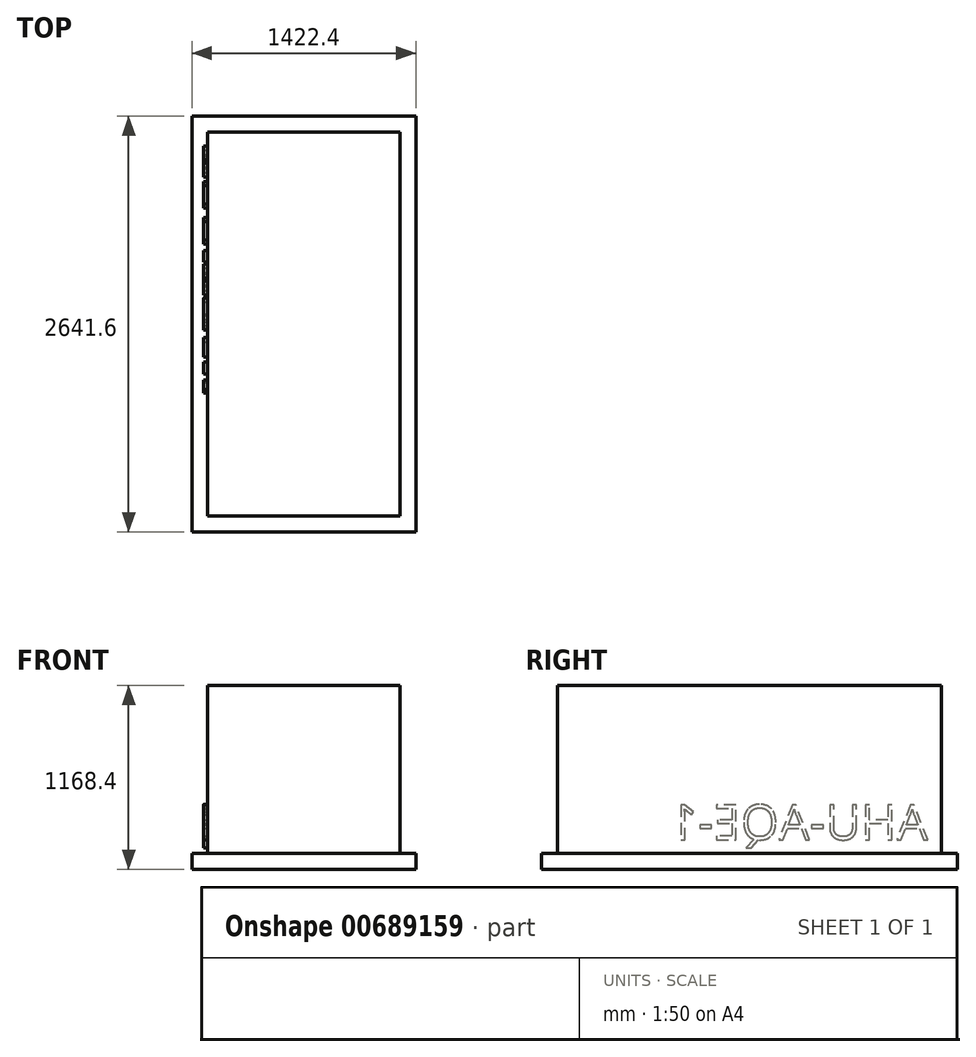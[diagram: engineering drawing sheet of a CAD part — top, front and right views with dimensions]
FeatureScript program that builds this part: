
annotation { "Feature Type Name" : "Feature", "Feature Type Description" : "" }
export const myFeature = defineFeature(function(context is Context, id is Id, definition is map)
    precondition{}
    {
        {
            var Q0;
            Q0=qCreatedBy(makeId("Front.planeOp"),FACE);
            var sketch = newSketch(context, id + "F0", { "sketchPlane" : qUnion([Q0])});
            skLineSegment(sketch, "E0.bottom", {"start": v(-67.53, 1048.52) * mm, "end": v(1151.67, 1048.52) * mm});
            skLineSegment(sketch, "E0.top", {"start": v(-67.53, -18.28) * mm, "end": v(1151.67, -18.28) * mm});
            skLineSegment(sketch, "E0.left", {"start": v(-67.53, 1048.52) * mm, "end": v(-67.53, -18.28) * mm});
            skLineSegment(sketch, "E0.right", {"start": v(1151.67, 1048.52) * mm, "end": v(1151.67, -18.28) * mm});
            skSolve(sketch);
        }
        {
            var Q0;
            Q0=makeQuery(id+"F0.imprint","IMPRINT",FACE,{"disambiguationData":[TD([[makeQuery(id+"F0.imprint","IMPRINT",EDGE,{"derivedFrom":sQuery(id+"F0.wireOp",EDGE,"E0.bottom")}),-1.0]])]});
            extrude(context, id + "F1", {"entities" : qUnion([Q0]), "depth" : 2438.4 * mm, "offsetDistance" : 25.4 * mm});
        }
        {
            var Q0;
            Q0=makeQuery(id+"F1.opExtrude","CAP_FACE",FACE,{"disambiguationData":[OSD([sQuery(id+"F0.wireOp",EDGE,"E0.bottom"),sQuery(id+"F0.wireOp",EDGE,"E0.top"),sQuery(id+"F0.wireOp",EDGE,"E0.left"),sQuery(id+"F0.wireOp",EDGE,"E0.right")])],"isStart":false});
            var sketch = newSketch(context, id + "F2", { "sketchPlane" : qUnion([Q0])});
            skLineSegment(sketch, "E1.bottom", {"start": v(-169.13, -18.28) * mm, "end": v(1253.27, -18.28) * mm});
            skLineSegment(sketch, "E1.top", {"start": v(-169.13, -119.88) * mm, "end": v(1253.27, -119.88) * mm});
            skLineSegment(sketch, "E1.left", {"start": v(-169.13, -18.28) * mm, "end": v(-169.13, -119.88) * mm});
            skLineSegment(sketch, "E1.right", {"start": v(1253.27, -18.28) * mm, "end": v(1253.27, -119.88) * mm});
            skSolve(sketch);
        }
        {
            var Q0;
            Q0=makeQuery(id+"F2.imprint","IMPRINT",FACE,{"disambiguationData":[TD([[makeQuery(id+"F2.imprint","IMPRINT",EDGE,{"derivedFrom":sQuery(id+"F2.wireOp",EDGE,"E1.top")}),1.0]])]});
            extrude(context, id + "F3", {"entities" : qUnion([Q0]), "oppositeDirection" : true, "depth" : 2540 * mm, "offsetDistance" : 25.4 * mm});
        }
        {
            var Q0;
            Q0=makeQuery(id+"F3.opExtrude","CAP_FACE",FACE,{"disambiguationData":[OSD([sQuery(id+"F2.wireOp",EDGE,"E1.bottom"),sQuery(id+"F2.wireOp",EDGE,"E1.top"),sQuery(id+"F2.wireOp",EDGE,"E1.left"),sQuery(id+"F2.wireOp",EDGE,"E1.right")])],"isStart":true});
            extrude(context, id + "F4", {"entities" : qUnion([Q0]), "operationType" : NewBodyOperationType.ADD, "depth" : 101.6 * mm, "offsetDistance" : 25.4 * mm});
        }
        {
            var Q0;
            Q0=makeQuery(id+"F1.opExtrude","SWEPT_FACE",FACE,{"disambiguationData":[OSD([sQuery(id+"F0.wireOp",EDGE,"E0.left")])]});
            var sketch = newSketch(context, id + "F5", { "sketchPlane" : qUnion([Q0])});
            skText(sketch, "E2", { "text": "AHU-AQE-1", "fontName": "OpenSans-Regular.ttf"});
            const initialGuessF5  = {"E2": [0.08868, 0.06892, 1, 0, 0.22307]};
            skSetInitialGuess(sketch, initialGuessF5);
            skSolve(sketch);
        }
        {
            var Q0;
            Q0 = qSketchRegion(id + "F5", true);
            extrude(context, id + "F6", {"entities" : qUnion([Q0]), "operationType" : NewBodyOperationType.ADD, "depth" : 25.4 * mm, "offsetDistance" : 25.4 * mm});
        }
    });
